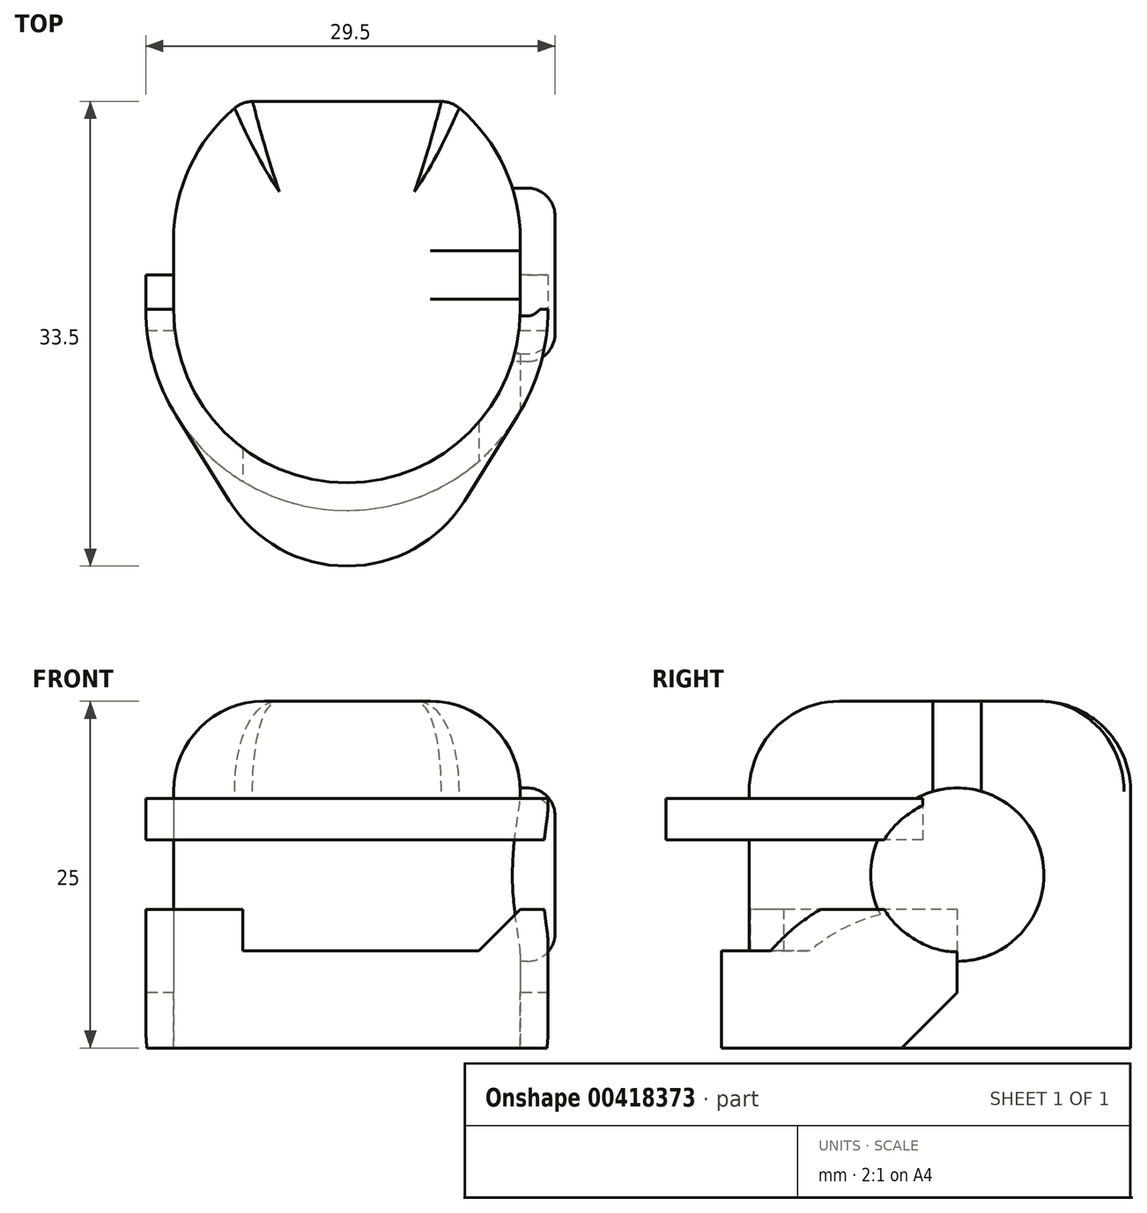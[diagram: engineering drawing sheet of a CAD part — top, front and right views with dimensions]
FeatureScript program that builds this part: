
annotation { "Feature Type Name" : "Feature", "Feature Type Description" : "" }
export const myFeature = defineFeature(function(context is Context, id is Id, definition is map)
    precondition{}
    {
        {
            var Q0;
            Q0=qCreatedBy(makeId("Top.planeOp"),FACE);
            var sketch = newSketch(context, id + "F0", { "sketchPlane" : qUnion([Q0])});
            skArc(sketch, "E0", {"start": v(-12.5, 0) * mm, "mid": v(0, -12.5) * mm, "end": v(12.5, 0) * mm});
            skLineSegment(sketch, "E1", {"start": v(12.5, 0) * mm, "end": v(12.5, 5) * mm});
            skLineSegment(sketch, "E2.MirrorCS", {"start": v(-12.5, 0) * mm, "end": v(-12.5, 5) * mm});
            skLineSegment(sketch, "E3", {"start": v(0, 15) * mm, "end": v(-7.5, 15) * mm});
            skArc(sketch, "E4", {"start": v(-7.5, 15) * mm, "mid": v(-11.18, 10.6) * mm, "end": v(-12.5, 5) * mm});
            skLineSegment(sketch, "E5.MirrorCS", {"start": v(0, 15) * mm, "end": v(7.5, 15) * mm});
            skArc(sketch, "E6.MirrorCS", {"start": v(7.5, 15) * mm, "mid": v(11.18, 10.6) * mm, "end": v(12.5, 5) * mm});
            skSolve(sketch);
        }
        {
            var Q0;
            Q0 = qSketchRegion(id + "F0", true);
            extrude(context, id + "F1", {"entities" : qUnion([Q0]), "depth" : 25 * mm, "offsetDistance" : 25 * mm});
        }
        {
            var Q0;
            Q0=makeQuery(id+"F1.opExtrude","SWEPT_FACE",FACE,{"disambiguationData":[OSD([sQuery(id+"F0.wireOp",EDGE,"E1")])]});
            var sketch = newSketch(context, id + "F2", { "sketchPlane" : qUnion([Q0])});
            skCircle(sketch, "E7", {"center": v(2.5, 12.5) * mm, "radius": 6.25 * mm});
            skPoint(sketch, "E7.centerSnap0", {"position": v(2.5, 0) * mm});
            skPoint(sketch, "E7.centerSnap1", {"position": v(5, 12.5) * mm});
            skSolve(sketch);
        }
        {
            var Q0;
            {var subQ0=sQuery(id+"F2.wireOp",EDGE,"E7");var subQ1=makeQuery(id+"F1.opExtrude","SWEPT_EDGE",EDGE,{"disambiguationData":[OSD([sQuery(id+"F0.wireOp",EDGE,"E0"),sQuery(id+"F0.wireOp",EDGE,"E1")])]});var subQ2=makeQuery(id+"F2.imprint","INTERSECT",VERTEX,{"disambiguationData":[OD(0.0)],"derivedFrom":[subQ1,subQ0]});Q0=makeQuery(id+"F2.imprint","IMPRINT",FACE,{"disambiguationData":[TD([[makeQuery(id+"F2.imprint","IMPRINT",EDGE,{"disambiguationData":[TD([[subQ2,-1.0]])],"derivedFrom":subQ0}),1.0]])]});}
            var Q1;
            {var subQ0=sQuery(id+"F2.wireOp",EDGE,"E7");var subQ1=makeQuery(id+"F1.opExtrude","SWEPT_EDGE",EDGE,{"disambiguationData":[OSD([sQuery(id+"F0.wireOp",EDGE,"E1"),sQuery(id+"F0.wireOp",EDGE,"E6.MirrorCS")])]});var subQ2=makeQuery(id+"F2.imprint","INTERSECT",VERTEX,{"disambiguationData":[OD(0.0)],"derivedFrom":[subQ1,subQ0]});Q1=makeQuery(id+"F2.imprint","IMPRINT",FACE,{"disambiguationData":[TD([[makeQuery(id+"F2.imprint","IMPRINT",EDGE,{"disambiguationData":[TD([[subQ2,1.0]])],"derivedFrom":subQ0}),1.0]])]});}
            var Q2;
            {var subQ0=sQuery(id+"F2.wireOp",EDGE,"E7");var subQ1=sQuery(id+"F0.wireOp",EDGE,"E1");var subQ2=makeQuery(id+"F1.opExtrude","SWEPT_EDGE",EDGE,{"disambiguationData":[OSD([sQuery(id+"F0.wireOp",EDGE,"E0"),subQ1])]});var subQ3=makeQuery(id+"F2.imprint","INTERSECT",VERTEX,{"disambiguationData":[OD(0.0)],"derivedFrom":[subQ2,subQ0]});Q2=makeQuery(id+"F2.imprint","IMPRINT",FACE,{"disambiguationData":[TD([[makeQuery(id+"F2.imprint","IMPRINT",EDGE,{"disambiguationData":[TD([[subQ3,1.0]])],"derivedFrom":subQ0}),1.0]])]});}
            extrude(context, id + "F3", {"entities" : qUnion([Q0, Q1, Q2]), "operationType" : NewBodyOperationType.ADD, "depth" : 2.5 * mm, "offsetDistance" : 25 * mm, "hasSecondDirection" : true, "secondDirectionOppositeDirection" : true, "secondDirectionDepth" : 2 * mm});
        }
        {
            var Q0;
            Q0=makeQuery(id+"F3.opExtrude","CAP_FACE",FACE,{"disambiguationData":[OSD([sQuery(id+"F2.wireOp",EDGE,"E7")])],"isStart":false});
            var Q1;
            Q1=makeQuery(id+"FZH5JUAWrRKBJOy_1.1.F3.opExtrude","CAP_FACE",FACE,{"disambiguationData":[OSD([sQuery(id+"F2.wireOp",EDGE,"E7")])],"isStart":false});
            var Q2;
            Q2=makeQuery(id+"F1.opExtrude","SWEPT_EDGE",EDGE,{"disambiguationData":[OSD([sQuery(id+"F0.wireOp",EDGE,"E5.MirrorCS"),sQuery(id+"F0.wireOp",EDGE,"E6.MirrorCS")])]});
            var Q3;
            Q3=makeQuery(id+"F1.opExtrude","SWEPT_EDGE",EDGE,{"disambiguationData":[OSD([sQuery(id+"F0.wireOp",EDGE,"E3"),sQuery(id+"F0.wireOp",EDGE,"E4")])]});
            fillet(context, id + "F4", {"entities" : qUnion([Q0, Q1, Q2, Q3]), "radius" : 2 * mm, "tangentPropagation" : true, "allowEdgeOverflow" : false});
        }
        {
            var Q0;
            Q0=makeQuery(id+"F1.opExtrude","CAP_FACE",FACE,{"disambiguationData":[OSD([sQuery(id+"F0.wireOp",EDGE,"E0"),sQuery(id+"F0.wireOp",EDGE,"E1"),sQuery(id+"F0.wireOp",EDGE,"E2.MirrorCS"),sQuery(id+"F0.wireOp",EDGE,"E3"),sQuery(id+"F0.wireOp",EDGE,"E4"),sQuery(id+"F0.wireOp",EDGE,"E5.MirrorCS"),sQuery(id+"F0.wireOp",EDGE,"E6.MirrorCS")])],"isStart":false});
            fillet(context, id + "F5", {"entities" : qUnion([Q0]), "radius" : 6.5 * mm, "tangentPropagation" : true, "allowEdgeOverflow" : false});
        }
        {
            var Q0;
            Q0=qCreatedBy(makeId("Top.planeOp"),FACE);
            var sketch = newSketch(context, id + "F6", { "sketchPlane" : qUnion([Q0])});
            skArc(sketch, "E8.0", {"start": v(-12.5, 0) * mm, "mid": v(0, -12.5) * mm, "end": v(12.5, 0) * mm});
            skLineSegment(sketch, "E9", {"start": v(-12.5, 0) * mm, "end": v(-14.5, 0) * mm});
            skArc(sketch, "E10", {"start": v(-14.5, 0) * mm, "mid": v(-10.25, -10.25) * mm, "end": v(0, -14.5) * mm});
            skArc(sketch, "E11.MirrorCS", {"start": v(14.5, 0) * mm, "mid": v(10.25, -10.25) * mm, "end": v(0, -14.5) * mm});
            skLineSegment(sketch, "E12.MirrorCS", {"start": v(12.5, 0) * mm, "end": v(14.5, 0) * mm});
            skLineSegment(sketch, "E13", {"start": v(-14.5, 0) * mm, "end": v(-14.5, 2.5) * mm});
            skLineSegment(sketch, "E14", {"start": v(-14.5, 2.5) * mm, "end": v(-12.5, 2.5) * mm});
            skLineSegment(sketch, "E15", {"start": v(-12.5, 2.5) * mm, "end": v(-12.5, 0) * mm});
            skLineSegment(sketch, "E16.MirrorCS", {"start": v(14.5, 0) * mm, "end": v(14.5, 2.5) * mm});
            skLineSegment(sketch, "E17.MirrorCS", {"start": v(12.5, 2.5) * mm, "end": v(12.5, 0) * mm});
            skLineSegment(sketch, "E18.MirrorCS", {"start": v(14.5, 2.5) * mm, "end": v(12.5, 2.5) * mm});
            skSolve(sketch);
        }
        {
            var Q0;
            Q0 = qSketchRegion(id + "F6", true);
            extrude(context, id + "F7", {"entities" : qUnion([Q0]), "operationType" : NewBodyOperationType.ADD, "depth" : 10 * mm, "offsetDistance" : 25 * mm});
        }
        {
            var Q0;
            Q0=makeQuery(id+"F7.opExtrude","CAP_EDGE",EDGE,{"disambiguationData":[OSD([sQuery(id+"F6.wireOp",EDGE,"E18.MirrorCS")])],"isStart":true});
            var Q1;
            Q1=makeQuery(id+"F7.opExtrude","CAP_EDGE",EDGE,{"disambiguationData":[OSD([sQuery(id+"F6.wireOp",EDGE,"E14")])],"isStart":true});
            chamfer(context, id + "F8", {"entities" : qUnion([Q0, Q1]), "width" : 4 * mm, "tangentPropagation" : true});
        }
        {
            var Q0;
            Q0=makeQuery(id+"F7.opExtrude","CAP_FACE",FACE,{"disambiguationData":[OSD([sQuery(id+"F6.wireOp",EDGE,"E8.0"),sQuery(id+"F6.wireOp",EDGE,"E10"),sQuery(id+"F6.wireOp",EDGE,"E11.MirrorCS"),sQuery(id+"F6.wireOp",EDGE,"E13"),sQuery(id+"F6.wireOp",EDGE,"E14"),sQuery(id+"F6.wireOp",EDGE,"E15"),sQuery(id+"F6.wireOp",EDGE,"E16.MirrorCS"),sQuery(id+"F6.wireOp",EDGE,"E17.MirrorCS"),sQuery(id+"F6.wireOp",EDGE,"E18.MirrorCS")])],"isStart":false});
            var sketch = newSketch(context, id + "F9", { "sketchPlane" : qUnion([Q0])});
            skArc(sketch, "E19.0", {"start": v(7.5, -10) * mm, "mid": v(0, -12.5) * mm, "end": v(-7.5, -10) * mm});
            skArc(sketch, "E20.0", {"start": v(-7.5, -12.4) * mm, "mid": v(0, -14.5) * mm, "end": v(7.5, -12.4) * mm});
            skLineSegment(sketch, "E21", {"start": v(-7.5, -10) * mm, "end": v(-7.5, -12.4) * mm});
            skLineSegment(sketch, "E22.MirrorCS", {"start": v(7.5, -10) * mm, "end": v(7.5, -12.4) * mm});
            skPoint(sketch, "E23.orphan", {"position": v(-12.5, 0) * mm});
            skPoint(sketch, "E24.orphan", {"position": v(-14.24, -2.76) * mm});
            skPoint(sketch, "E25.orphan", {"position": v(12.5, 0) * mm});
            skPoint(sketch, "E26.orphan", {"position": v(14.24, -2.76) * mm});
            skSolve(sketch);
        }
        {
            var Q0;
            Q0 = qSketchRegion(id + "F9", true);
            extrude(context, id + "F10", {"entities" : qUnion([Q0]), "operationType" : NewBodyOperationType.REMOVE, "oppositeDirection" : true, "depth" : 3 * mm, "offsetDistance" : 25 * mm});
        }
        {
            var Q0;
            Q0=makeQuery(id+"F10.boolean.opBoolean","COPY",EDGE,{"derivedFrom":makeQuery(id+"F10.opExtrude","CAP_EDGE",EDGE,{"disambiguationData":[OSD([sQuery(id+"F9.wireOp",EDGE,"E21")])],"isStart":true})});
            var Q1;
            Q1=makeQuery(id+"F10.boolean.opBoolean","COPY",EDGE,{"derivedFrom":makeQuery(id+"F10.opExtrude","CAP_EDGE",EDGE,{"disambiguationData":[OSD([sQuery(id+"F9.wireOp",EDGE,"E22.MirrorCS")])],"isStart":true})});
            chamfer(context, id + "F11", {"entities" : qUnion([Q0, Q1]), "width" : 5 * mm, "tangentPropagation" : true});
        }
        {
            var Q0;
            Q0=qCreatedBy(makeId("Top.planeOp"),FACE);
            cPlane(context, id + "F12", {"entities" : qUnion([Q0]), "cplaneType" : CPlaneType.OFFSET, "offset" : 15 * mm, "width" : 150 * mm, "height" : 150 * mm});
        }
        {
            var Q0;
            Q0=qCreatedBy(id+"F12.planeOp",FACE);
            var sketch = newSketch(context, id + "F13", { "sketchPlane" : qUnion([Q0])});
            skArc(sketch, "E27.0", {"start": v(12.5, 0) * mm, "mid": v(0, -12.5) * mm, "end": v(-12.5, 0) * mm});
            skArc(sketch, "E28", {"start": v(-9.75, -10.74) * mm, "mid": v(0, -18.5) * mm, "end": v(9.75, -10.74) * mm});
            skArc(sketch, "E29", {"start": v(-14.5, 0) * mm, "mid": v(-10.25, -10.25) * mm, "end": v(0, -14.5) * mm});
            skLineSegment(sketch, "E30", {"start": v(-14.5, 0) * mm, "end": v(-12.5, 0) * mm});
            skLineSegment(sketch, "E31.MirrorCS", {"start": v(14.5, 0) * mm, "end": v(12.5, 0) * mm});
            skArc(sketch, "E32.MirrorCS", {"start": v(14.5, 0) * mm, "mid": v(10.25, -10.25) * mm, "end": v(0, -14.5) * mm});
            skLineSegment(sketch, "E33", {"start": v(-8.48, -13.8) * mm, "end": v(-12.3, -7.68) * mm});
            skLineSegment(sketch, "E34.MirrorCS", {"start": v(8.48, -13.8) * mm, "end": v(12.3, -7.68) * mm});
            skSolve(sketch);
        }
        {
            var Q0;
            Q0 = qSketchRegion(id + "F13", true);
            extrude(context, id + "F14", {"entities" : qUnion([Q0]), "operationType" : NewBodyOperationType.ADD, "depth" : 3 * mm, "offsetDistance" : 25 * mm});
        }
    });
